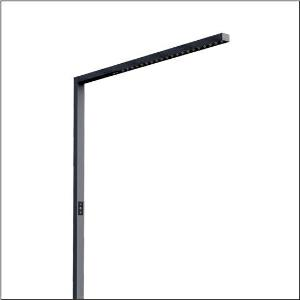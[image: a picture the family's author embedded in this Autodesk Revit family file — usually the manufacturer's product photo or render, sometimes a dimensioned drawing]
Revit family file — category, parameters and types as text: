
# Revit family: silica_31_floor_51my52fa4cb
name_source: partatom
category: Lighting Fixtures
units: mm (PartAtom-declared; Revit-internal decimal feet)

## family parameters
Cut with Voids When Loaded = No
Host = Face
Light Source = No
Part Type = Normal
Room Calculation Point = No
Round Connector Dimension = Use Diameter
Shared = No

## types (1)
- Silica 31 Floor (1 x LED, 10600 lm, 75 W, 4000K)
    Apparent Load = 75 VA
    CIE Flux Codes = 86 100 100 24 100
    Color Rendering = 80
    Color Temperature = 4000K
    Default Elevation = 1800 mm
    Description = Silica® 31 Floor, floorstanding luminaire, secondary optical cover: cover panel, of PMMA, light emission: direct/indirect distribution, primary light characteristic: symmetric, installation type: not mounted, LED, rated luminous flux: 10.600lm, luminous efficacy: 141lm/W, light colour: 840, colour temperature: 4000K, control gear: Touchdim, daylight-dependent control, with cable with plug, mains connection: 230V, AC, 50Hz, connection cable included, cable length: 2,5m, rated input power: 75W, luminaire head, of aluminium, jet black (RAL 9005), length: 1.203mm, width: 52mm, supporting column, angular, of aluminium, jet black (RAL 9005), baseplate, of steel, jet black (RAL 9005), local control - self-sufficient standalone sensors, direct and indirect component separately switchable, protection rating (complete): IP20, insulation class (complete): insulation class I (protective earthing), certification: CE, ENEC, permissible operating ambient temperature: -20..+40°C, standard: EN 50419, packaging unit: 1 piece
    Height = 36 mm
    Lamp = 1 x LED
    Lamp Light Flux = 10600 lm
    Lamp Power = 75 W
    Lamp count = 1
    Length = 1203 mm
    Luminous efficacy = 141 lm/W
    Manufacturer = Siteco
    ModVariant = No
    Model = 51MY52FA4CB
    Mounting Place = Floor
    Mounting Type = Freestanding
    Number of Poles = 1
    OnlyDefault = Yes
    Power Factor = 1
    Product Name = Silica 31 Floor
    Product group = floorstanding luminaire
    ProductGroupID = 1302
    Protection Class = Protection class I
    Protection Degree = IP 20
    RLX_Detail_Level = 1
    RLX_Emergency_Light_Flux = 0 lm
    RLX_Emergency_Type = 0
    RLX_Emergency_Type_DB = No
    RlxData = <blob elided: 20277 chars, md5=04bb5897>
    Socket = socket
    Standby Power = 0 W
    System Light Flux = 10600 lm
    System Power = 75 W
    Type Comments = Product without accessories
    Type Image = l_1275297.jpg
    URL = http://relux.com
    VarID = ---
    Voltage = 0 V
    Weight = 0.00 kg
    Width = 52 mm  [stored 0.170604 ft]

note: [stored X ft] marks values corroborated as IEEE doubles in the binary element streams (Revit-internal decimal feet)

## geometry (parser evidence)
native form markers: Blend x4, Sweep x13
no freeform markers — native parametric forms only
